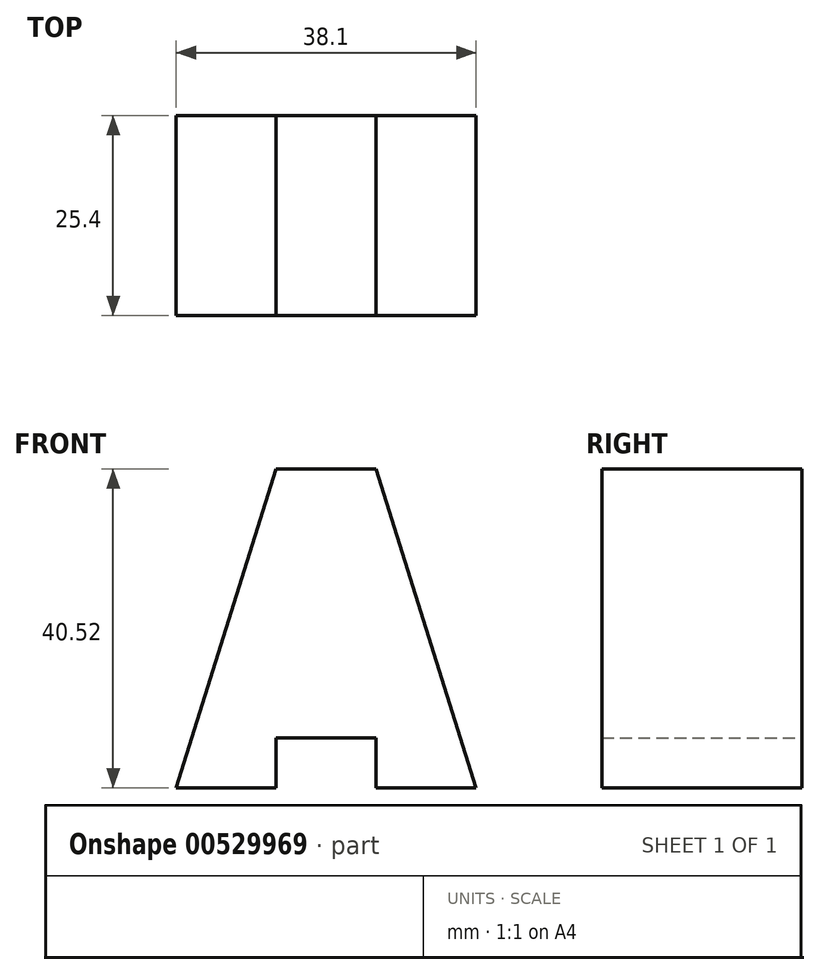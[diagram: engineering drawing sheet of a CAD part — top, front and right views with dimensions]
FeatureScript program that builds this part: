
annotation { "Feature Type Name" : "Feature", "Feature Type Description" : "" }
export const myFeature = defineFeature(function(context is Context, id is Id, definition is map)
    precondition{}
    {
        {
            var Q0;
            Q0=qCreatedBy(makeId("Front.planeOp"),FACE);
            var sketch = newSketch(context, id + "F0", { "sketchPlane" : qUnion([Q0])});
            skLineSegment(sketch, "E0", {"start": v(-53.94, 49.5) * mm, "end": v(-41.24, 49.5) * mm});
            skLineSegment(sketch, "E1", {"start": v(-53.94, 15.34) * mm, "end": v(-41.24, 15.34) * mm});
            skLineSegment(sketch, "E2", {"start": v(-53.94, 49.5) * mm, "end": v(-66.64, 8.99) * mm});
            skLineSegment(sketch, "E3", {"start": v(-66.64, 8.99) * mm, "end": v(-53.94, 8.99) * mm});
            skLineSegment(sketch, "E4", {"start": v(-53.94, 15.34) * mm, "end": v(-53.94, 8.99) * mm});
            skLineSegment(sketch, "E5", {"start": v(-41.24, 15.34) * mm, "end": v(-41.24, 8.99) * mm});
            skLineSegment(sketch, "E6", {"start": v(-41.24, 8.99) * mm, "end": v(-28.54, 8.99) * mm});
            skLineSegment(sketch, "E7", {"start": v(-41.24, 49.5) * mm, "end": v(-28.54, 8.99) * mm});
            skSolve(sketch);
        }
        {
            var Q0;
            Q0 = qSketchRegion(id + "F0", true);
            extrude(context, id + "F1", {"entities" : qUnion([Q0]), "depth" : 25.4 * mm, "offsetDistance" : 25.4 * mm});
        }
    });
